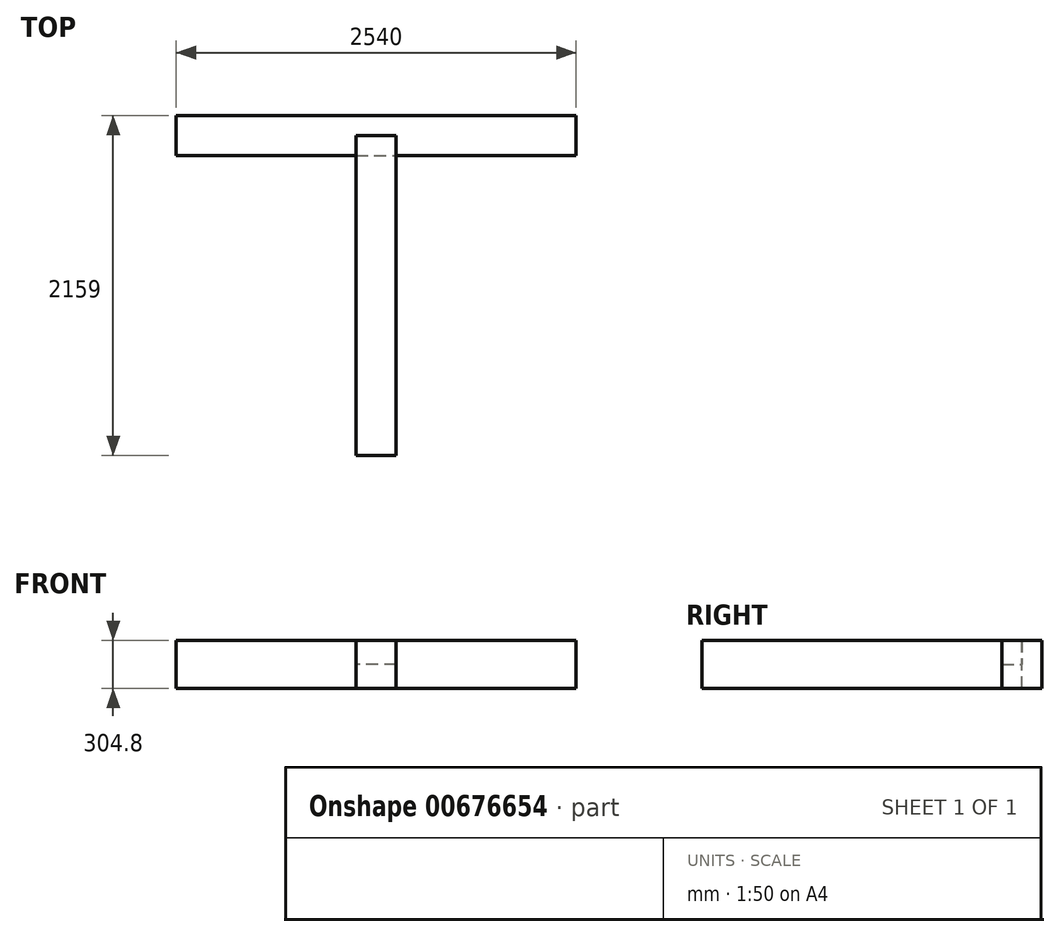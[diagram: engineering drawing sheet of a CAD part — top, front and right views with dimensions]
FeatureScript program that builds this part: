
annotation { "Feature Type Name" : "Feature", "Feature Type Description" : "" }
export const myFeature = defineFeature(function(context is Context, id is Id, definition is map)
    precondition{}
    {
        {
            var Q0;
            Q0=qCreatedBy(makeId("Top.planeOp"),FACE);
            var sketch = newSketch(context, id + "F0", { "sketchPlane" : qUnion([Q0])});
            skLineSegment(sketch, "E0.bottom", {"start": v(-1270, 254) * mm, "end": v(1270, 254) * mm});
            skLineSegment(sketch, "E0.top", {"start": v(-1270, 0) * mm, "end": v(1270, 0) * mm});
            skLineSegment(sketch, "E0.left", {"start": v(-1270, 254) * mm, "end": v(-1270, 0) * mm});
            skLineSegment(sketch, "E0.right", {"start": v(1270, 254) * mm, "end": v(1270, 0) * mm});
            skSolve(sketch);
        }
        {
            var Q0;
            Q0 = qSketchRegion(id + "F0", true);
            extrude(context, id + "F1", {"entities" : qUnion([Q0]), "depth" : 304.8 * mm, "offsetDistance" : 25.4 * mm});
        }
        {
            var Q0;
            Q0=makeQuery(id+"F1.opExtrude","CAP_FACE",FACE,{"disambiguationData":[OSD([sQuery(id+"F0.wireOp",EDGE,"E0.bottom"),sQuery(id+"F0.wireOp",EDGE,"E0.top"),sQuery(id+"F0.wireOp",EDGE,"E0.left"),sQuery(id+"F0.wireOp",EDGE,"E0.right")])],"isStart":false});
            var sketch = newSketch(context, id + "F2", { "sketchPlane" : qUnion([Q0])});
            skLineSegment(sketch, "E1.bottom", {"start": v(-127, 127) * mm, "end": v(127, 127) * mm});
            skLineSegment(sketch, "E1.top", {"start": v(-127, 0) * mm, "end": v(127, 0) * mm});
            skLineSegment(sketch, "E1.left", {"start": v(-127, 127) * mm, "end": v(-127, 0) * mm});
            skLineSegment(sketch, "E1.right", {"start": v(127, 127) * mm, "end": v(127, 0) * mm});
            skSolve(sketch);
        }
        {
            var Q0;
            Q0 = qSketchRegion(id + "F2", true);
            extrude(context, id + "F3", {"entities" : qUnion([Q0]), "operationType" : NewBodyOperationType.REMOVE, "oppositeDirection" : true, "depth" : 152.4 * mm, "offsetDistance" : 25.4 * mm});
        }
        {
            var Q0;
            Q0=qCreatedBy(makeId("Top.planeOp"),FACE);
            var sketch = newSketch(context, id + "F4", { "sketchPlane" : qUnion([Q0])});
            skLineSegment(sketch, "E2.bottom", {"start": v(-127, -1905) * mm, "end": v(127, -1905) * mm});
            skLineSegment(sketch, "E2.top", {"start": v(-127, 127) * mm, "end": v(127, 127) * mm});
            skLineSegment(sketch, "E2.left", {"start": v(-127, -1905) * mm, "end": v(-127, 127) * mm});
            skLineSegment(sketch, "E2.right", {"start": v(127, -1905) * mm, "end": v(127, 127) * mm});
            skPoint(sketch, "E3.0", {"position": v(-127, 127) * mm});
            skPoint(sketch, "E4.0", {"position": v(127, 127) * mm});
            skSolve(sketch);
        }
        {
            var Q0;
            Q0 = qSketchRegion(id + "F4", true);
            extrude(context, id + "F5", {"entities" : qUnion([Q0]), "depth" : 304.8 * mm, "offsetDistance" : 25.4 * mm});
        }
        {
            var Q0;
            Q0=makeQuery(id+"F5.opExtrude","SWEPT_FACE",FACE,{"disambiguationData":[OSD([sQuery(id+"F4.wireOp",EDGE,"E2.top")])]});
            var sketch = newSketch(context, id + "F6", { "sketchPlane" : qUnion([Q0])});
            skLineSegment(sketch, "E5.bottom", {"start": v(-127, 0) * mm, "end": v(127, 0) * mm});
            skLineSegment(sketch, "E5.top", {"start": v(-127, 152.4) * mm, "end": v(127, 152.4) * mm});
            skLineSegment(sketch, "E5.left", {"start": v(-127, 0) * mm, "end": v(-127, 152.4) * mm});
            skLineSegment(sketch, "E5.right", {"start": v(127, 0) * mm, "end": v(127, 152.4) * mm});
            skSolve(sketch);
        }
        {
            var Q0;
            Q0 = qSketchRegion(id + "F6", true);
            extrude(context, id + "F7", {"entities" : qUnion([Q0]), "operationType" : NewBodyOperationType.REMOVE, "oppositeDirection" : true, "depth" : 127 * mm, "offsetDistance" : 25.4 * mm});
        }
    });
